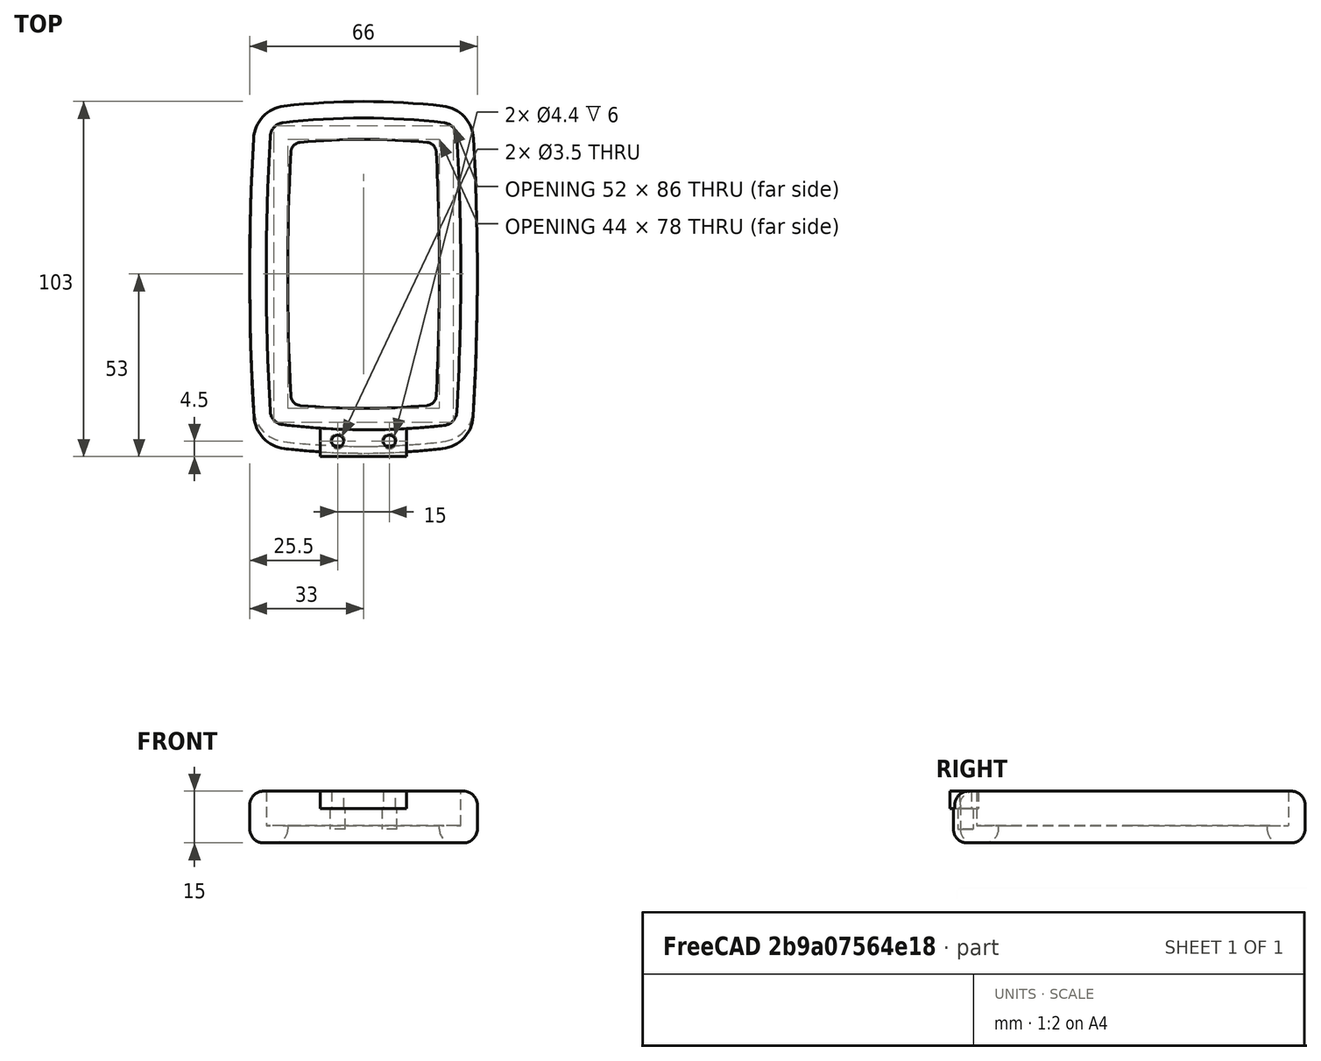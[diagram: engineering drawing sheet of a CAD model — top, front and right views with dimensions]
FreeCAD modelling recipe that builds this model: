
FCSTD DOCUMENT  (FreeCAD 0.20R29603 (Git))
Label: pad
License: All rights reserved
LicenseURL: http://en.wikipedia.org/wiki/All_rights_reserved
objects: Part::Cylinder×37, Part::MultiCommon×33, Part::Box×9, Part::Cut×8, Part::Fillet×7, Part::MultiFuse×2, Spreadsheet::Sheet×1, Mesh::Feature×1
note: 96 computed .brp shape members not serialized (recipe doc carries the construction recipe); baked Part::Feature solids carry a one-line shape summary decoded from their .brp

FEATURE [Part::Box] Box  label="Cube"
  AttacherType = Attacher::AttachEngine3D
  Height = 29
  Length = 60
  Placement = pos=(-29.77,-50.31,14) rot=(0,0,1;0rad)
  Width = 99
FEATURE [Part::Cylinder] Cylinder  label="Long Side circle"
  Angle = 360
  AttacherType = Attacher::AttachEngine3D
  FirstAngle = 0
  Height = 36
  Placement = pos=(671.8,0,0) rot=(0,0,1;0rad)
  Radius = 700
  SecondAngle = 0
  expr: .Placement.Base.x = Spreadsheet.B1 - 54 / 2 - Spreadsheet.B9
  expr: Radius = Spreadsheet.B1
FEATURE [Part::Cylinder] Cylinder001  label="Short side circle"
  Angle = 360
  AttacherType = Attacher::AttachEngine3D
  FirstAngle = 0
  Height = 53
  Placement = pos=(1,154.8,0) rot=(0,0,1;0rad)
  Radius = 200
  SecondAngle = 0
  expr: .Placement.Base.y = Spreadsheet.B2 - 88 / 2 - Spreadsheet.B9
  expr: Radius = Spreadsheet.B2
FEATURE [Part::MultiCommon] Common
  Shapes = -> [Box,Cylinder001]
FEATURE [Part::Cylinder] Cylinder002  label="Short side circle001"
  Angle = 360
  AttacherType = Attacher::AttachEngine3D
  FirstAngle = 0
  Height = 77
  Placement = pos=(-32,1,-262.75) rot=(0,1,0;1.5708rad)
  Radius = 310
  SecondAngle = 0
  expr: .Placement.Base.z = -(Spreadsheet.B3 - 31.25) + 16
  expr: Radius = Spreadsheet.B3
FEATURE [Part::MultiCommon] Common001
  Shapes = -> [Cylinder002,Common]
FEATURE [Part::MultiCommon] Common002
  Shapes = -> [Cylinder,Common001]
FEATURE [Part::Cylinder] Cylinder003  label="Short side circle002"
  Angle = 360
  AttacherType = Attacher::AttachEngine3D
  FirstAngle = 0
  Height = 36
  Placement = pos=(0,-154.8,0) rot=(0,0,1;0rad)
  Radius = 200
  SecondAngle = 0
  expr: .Placement.Base.y = -(Spreadsheet.B2 - 88 / 2) + Spreadsheet.B9
  expr: Radius = Spreadsheet.B2
FEATURE [Part::Cylinder] Cylinder004  label="Long Side circle001"
  Angle = 360
  AttacherType = Attacher::AttachEngine3D
  FirstAngle = 0
  Height = 36
  Placement = pos=(-671.8,0,0) rot=(0,0,1;0rad)
  Radius = 700
  SecondAngle = 0
  expr: .Placement.Base.x = -(Spreadsheet.B1 - 54 / 2) + Spreadsheet.B9
  expr: Radius = Spreadsheet.B1
FEATURE [Part::MultiCommon] Common003
  Shapes = -> [Cylinder004,Common002]
FEATURE [Part::MultiCommon] Common004
  Shapes = -> [Common003,Cylinder003]
FEATURE [Spreadsheet::Sheet] Spreadsheet
  cells = A1=long side; B1=700; F1=pad long side; G1=750; A2=short side; B2=200; F2=pad short side; G2=250; A3=top; B3=310; A4=center hole; B4=66; C4=27; D4=5; A5=Screw; B5=6.5; C5=3.5; A6=Screw head height; B6=3; A7=THreaded insert; B7=4.4; A9=earmuff margin; B9=1.2; A10=screwhole dist; B10=15
FEATURE [Part::Box] Box001  label="Cube001"
  AttacherType = Attacher::AttachEngine3D
  Height = 36
  Length = 60
  Placement = pos=(-29.77,-50.31,14) rot=(0,0,1;0rad)
  Width = 99
FEATURE [Part::Cylinder] Cylinder005  label="Long Side circle002"
  Angle = 360
  AttacherType = Attacher::AttachEngine3D
  FirstAngle = 0
  Height = 36
  Placement = pos=(678,0,0) rot=(0,0,1;0rad)
  Radius = 700
  SecondAngle = 0
  expr: .Placement.Base.x = Spreadsheet.B1 - 54 / 2 + 5
  expr: Radius = Spreadsheet.B1
FEATURE [Part::Cylinder] Cylinder006  label="Short side circle003"
  Angle = 360
  AttacherType = Attacher::AttachEngine3D
  FirstAngle = 0
  Height = 53
  Placement = pos=(0,161,0) rot=(0,0,1;0rad)
  Radius = 200
  SecondAngle = 0
  expr: .Placement.Base.y = Spreadsheet.B2 - 88 / 2 + 5
  expr: Radius = Spreadsheet.B2
FEATURE [Part::MultiCommon] Common005
  Shapes = -> [Box001,Cylinder006]
FEATURE [Part::Cylinder] Cylinder007  label="Short side circle004"
  Angle = 360
  AttacherType = Attacher::AttachEngine3D
  FirstAngle = 0
  Height = 77
  Placement = pos=(-32,0,0) rot=(0,1,0;1.5708rad)
  Radius = 310
  SecondAngle = 0
  expr: Radius = Spreadsheet.B3
FEATURE [Part::MultiCommon] Common006
  Shapes = -> [Cylinder007,Common005]
FEATURE [Part::MultiCommon] Common007
  Shapes = -> [Cylinder005,Common006]
FEATURE [Part::Cylinder] Cylinder008  label="Short side circle005"
  Angle = 360
  AttacherType = Attacher::AttachEngine3D
  FirstAngle = 0
  Height = 36
  Placement = pos=(0,-161,0) rot=(0,0,1;0rad)
  Radius = 200
  SecondAngle = 0
  expr: .Placement.Base.y = -(Spreadsheet.B2 - 88 / 2) - 5
  expr: Radius = Spreadsheet.B2
FEATURE [Part::Cylinder] Cylinder009  label="Long Side circle003"
  Angle = 360
  AttacherType = Attacher::AttachEngine3D
  FirstAngle = 0
  Height = 36
  Placement = pos=(-678,0,0) rot=(0,0,1;0rad)
  Radius = 700
  SecondAngle = 0
  expr: .Placement.Base.x = -(Spreadsheet.B1 - 54 / 2) - 5
  expr: Radius = Spreadsheet.B1
FEATURE [Part::MultiCommon] Common008
  Shapes = -> [Cylinder009,Common007]
FEATURE [Part::MultiCommon] Common009
  Shapes = -> [Common008,Cylinder008]
FEATURE [Mesh::Feature] Sccouter_Pad
  Placement = pos=(-33,50,-6) rot=(-1,0,0;4.71239rad)
FEATURE [Part::Fillet] Fillet  label="Center hole"
  Base = -> Common009
  Edges = 4 edges r=3: [Edge3,Edge5,Edge11,Edge15]
FEATURE [Part::Fillet] Fillet001  label="Pad cut"
  Base = -> Common004
  Edges = 4 edges r=4.2: [Edge3,Edge5,Edge11,Edge15]
  Placement = pos=(0,0,-15) rot=(0,0,1;0rad)
FEATURE [Part::Cylinder] Cylinder010  label="Short side circle006"
  Angle = 360
  AttacherType = Attacher::AttachEngine3D
  FirstAngle = 0
  Height = 36
  Placement = pos=(0,-150,0) rot=(0,0,1;0rad)
  Radius = 200
  SecondAngle = 0
  expr: .Placement.Base.y = -(Spreadsheet.G2 - 200 / 2)
  expr: Radius = Spreadsheet.B2
FEATURE [Part::Cylinder] Cylinder011  label="Long Side circle004"
  Angle = 360
  AttacherType = Attacher::AttachEngine3D
  FirstAngle = 0
  Height = 36
  Placement = pos=(-667,0,0) rot=(0,0,1;0rad)
  Radius = 700
  SecondAngle = 0
  expr: .Placement.Base.x = -(Spreadsheet.G1 - 166 / 2)
  expr: Radius = Spreadsheet.B1
FEATURE [Part::Cylinder] Cylinder012  label="Long Side circle005"
  Angle = 360
  AttacherType = Attacher::AttachEngine3D
  FirstAngle = 0
  Height = 36
  Placement = pos=(667,0,0) rot=(0,0,1;0rad)
  Radius = 700
  SecondAngle = 0
  expr: .Placement.Base.x = Spreadsheet.G1 - 166 / 2
  expr: Radius = Spreadsheet.B1
FEATURE [Part::Cylinder] Cylinder013  label="Short side circle007"
  Angle = 360
  AttacherType = Attacher::AttachEngine3D
  FirstAngle = 0
  Height = 53
  Placement = pos=(0,148,0) rot=(0,0,1;0rad)
  Radius = 200
  SecondAngle = 0
  expr: .Placement.Base.y = Spreadsheet.G2 - 200 / 2 - 2
  expr: Radius = Spreadsheet.B2
FEATURE [Part::Box] Box002  label="Cube002"
  AttacherType = Attacher::AttachEngine3D
  Height = 15
  Length = 110
  Placement = pos=(-48,-60,11) rot=(0,0,1;0rad)
  Width = 300
FEATURE [Part::MultiCommon] Common010
  Shapes = -> [Box002,Cylinder013]
FEATURE [Part::MultiCommon] Common011
  Shapes = -> [Cylinder012,Common010]
FEATURE [Part::MultiCommon] Common012
  Shapes = -> [Cylinder011,Common011]
FEATURE [Part::MultiCommon] Common013
  Placement = pos=(0,0,6) rot=(0,0,1;0rad)
  Shapes = -> [Common012,Cylinder010]
FEATURE [Part::Cut] Cut
  Base = -> Common013
  Placement = pos=(0,0,-23) rot=(0,0,1;0rad)
  Tool = -> Fillet
FEATURE [Part::Fillet] Fillet002
  Base = -> Cut
  Edges = 23 edges: [Edge2 r=4,Edge3 r=10,Edge4 r=4,Edge5 r=10,Edge6 r=4,Edge7 r=4,Edge8 r=4,Edge9 r=4,Edge10 r=4,Edge20 r=10,Edge21 r=4,Edge22 r=4,Edge23 r=4,Edge24 r=4,Edge25 r=4,Edge26 r=4,Edge27 r=4,Edge28 r=4,Edge29 r=4,Edge30 r=4,Edge31 r=4,Edge32 r=4,Edge33 r=10]
FEATURE [Part::Cut] Cut001  label="Pad pre cuts"
  Base = -> Fillet002
  Tool = -> Fillet001
FEATURE [Part::Cylinder] Cylinder014  label="Cylinder"
  Angle = 360
  AttacherType = Attacher::AttachEngine3D
  FirstAngle = 0
  Height = 10
  Placement = pos=(7.5,-47.5,0) rot=(0,0,1;0rad)
  Radius = 2.2
  SecondAngle = 0
  expr: .Placement.Base.x = Spreadsheet.B10 / 2
  expr: Radius = Spreadsheet.B7 / 2
FEATURE [Part::Cylinder] Cylinder015
  Angle = 360
  AttacherType = Attacher::AttachEngine3D
  FirstAngle = 0
  Height = 10
  Placement = pos=(-7.5,-47.5,0) rot=(0,0,1;0rad)
  Radius = 2.2
  SecondAngle = 0
  expr: .Placement.Base.x = -Spreadsheet.B10 / 2
  expr: Radius = Spreadsheet.B7 / 2
FEATURE [Part::MultiFuse] Fusion  label="Screw holes"
  Placement = pos=(0,-1,-2) rot=(0,0,1;0rad)
  Shapes = -> [Cylinder015,Cylinder014]
FEATURE [Part::Box] Box003  label="Cube003"
  AttacherType = Attacher::AttachEngine3D
  Height = 10
  Length = 25
  Placement = pos=(-12.5,-53,4) rot=(0,0,1;0rad)
  Width = 10
  expr: .Placement.Base.x = -(Spreadsheet.B10 + 10) / 2
  expr: Length = Spreadsheet.B10 + 10
FEATURE [Part::Box] Box004  label="Cube004"
  AttacherType = Attacher::AttachEngine3D
  Height = 5
  Length = 25
  Placement = pos=(-12.5,-53,4) rot=(0,0,1;0rad)
  Width = 10
  expr: .Placement.Base.x = -(Spreadsheet.B10 + 10) / 2
  expr: Length = Spreadsheet.B10 + 10
FEATURE [Part::Cut] Cut002
  Base = -> Cut001
  Tool = -> Box003
FEATURE [Part::Box] Box005  label="Cube005"
  AttacherType = Attacher::AttachEngine3D
  Height = 29
  Length = 60
  Placement = pos=(-29.77,-50.31,14) rot=(0,0,1;0rad)
  Width = 99
FEATURE [Part::Box] Box006  label="Cube006"
  AttacherType = Attacher::AttachEngine3D
  Height = 36
  Length = 60
  Placement = pos=(-29.77,-50.31,14) rot=(0,0,1;0rad)
  Width = 99
FEATURE [Part::Box] Box007  label="Cube007"
  AttacherType = Attacher::AttachEngine3D
  Height = 15
  Length = 110
  Placement = pos=(-48,-51,11) rot=(0,0,1;0rad)
  Width = 122
FEATURE [Part::Cylinder] Cylinder016  label="Long Side circle006"
  Angle = 360
  AttacherType = Attacher::AttachEngine3D
  FirstAngle = 0
  Height = 36
  Placement = pos=(671.8,0,0) rot=(0,0,1;0rad)
  Radius = 700
  SecondAngle = 0
  expr: .Placement.Base.x = Spreadsheet.B1 - 54 / 2 - Spreadsheet.B9
  expr: Radius = Spreadsheet.B1
FEATURE [Part::Cylinder] Cylinder017  label="Short side circle008"
  Angle = 360
  AttacherType = Attacher::AttachEngine3D
  FirstAngle = 0
  Height = 53
  Placement = pos=(1,154.8,0) rot=(0,0,1;0rad)
  Radius = 200
  SecondAngle = 0
  expr: .Placement.Base.y = Spreadsheet.B2 - 88 / 2 - Spreadsheet.B9
  expr: Radius = Spreadsheet.B2
FEATURE [Part::MultiCommon] Common014
  Shapes = -> [Box005,Cylinder017]
FEATURE [Part::Cylinder] Cylinder018  label="Short side circle009"
  Angle = 360
  AttacherType = Attacher::AttachEngine3D
  FirstAngle = 0
  Height = 77
  Placement = pos=(-32,1,-262.75) rot=(0,1,0;1.5708rad)
  Radius = 310
  SecondAngle = 0
  expr: .Placement.Base.z = -(Spreadsheet.B3 - 31.25) + 16
  expr: Radius = Spreadsheet.B3
FEATURE [Part::MultiCommon] Common015
  Shapes = -> [Cylinder018,Common014]
FEATURE [Part::MultiCommon] Common016
  Shapes = -> [Cylinder016,Common015]
FEATURE [Part::Cylinder] Cylinder019  label="Short side circle010"
  Angle = 360
  AttacherType = Attacher::AttachEngine3D
  FirstAngle = 0
  Height = 36
  Placement = pos=(0,-154.8,0) rot=(0,0,1;0rad)
  Radius = 200
  SecondAngle = 0
  expr: .Placement.Base.y = -(Spreadsheet.B2 - 88 / 2) + Spreadsheet.B9
  expr: Radius = Spreadsheet.B2
FEATURE [Part::Cylinder] Cylinder020  label="Long Side circle007"
  Angle = 360
  AttacherType = Attacher::AttachEngine3D
  FirstAngle = 0
  Height = 36
  Placement = pos=(-671.8,0,0) rot=(0,0,1;0rad)
  Radius = 700
  SecondAngle = 0
  expr: .Placement.Base.x = -(Spreadsheet.B1 - 54 / 2) + Spreadsheet.B9
  expr: Radius = Spreadsheet.B1
FEATURE [Part::MultiCommon] Common017
  Shapes = -> [Cylinder020,Common016]
FEATURE [Part::MultiCommon] Common018
  Shapes = -> [Common017,Cylinder019]
FEATURE [Part::Cylinder] Cylinder021  label="Long Side circle008"
  Angle = 360
  AttacherType = Attacher::AttachEngine3D
  FirstAngle = 0
  Height = 36
  Placement = pos=(678,0,0) rot=(0,0,1;0rad)
  Radius = 700
  SecondAngle = 0
  expr: .Placement.Base.x = Spreadsheet.B1 - 54 / 2 + 5
  expr: Radius = Spreadsheet.B1
FEATURE [Part::Cylinder] Cylinder022  label="Short side circle011"
  Angle = 360
  AttacherType = Attacher::AttachEngine3D
  FirstAngle = 0
  Height = 53
  Placement = pos=(0,161,0) rot=(0,0,1;0rad)
  Radius = 200
  SecondAngle = 0
  expr: .Placement.Base.y = Spreadsheet.B2 - 88 / 2 + 5
  expr: Radius = Spreadsheet.B2
FEATURE [Part::MultiCommon] Common019
  Shapes = -> [Box006,Cylinder022]
FEATURE [Part::Cylinder] Cylinder023  label="Short side circle012"
  Angle = 360
  AttacherType = Attacher::AttachEngine3D
  FirstAngle = 0
  Height = 77
  Placement = pos=(-32,0,0) rot=(0,1,0;1.5708rad)
  Radius = 310
  SecondAngle = 0
  expr: Radius = Spreadsheet.B3
FEATURE [Part::MultiCommon] Common020
  Shapes = -> [Cylinder023,Common019]
FEATURE [Part::MultiCommon] Common021
  Shapes = -> [Cylinder021,Common020]
FEATURE [Part::Cylinder] Cylinder024  label="Short side circle013"
  Angle = 360
  AttacherType = Attacher::AttachEngine3D
  FirstAngle = 0
  Height = 36
  Placement = pos=(0,-161,0) rot=(0,0,1;0rad)
  Radius = 200
  SecondAngle = 0
  expr: .Placement.Base.y = -(Spreadsheet.B2 - 88 / 2) - 5
  expr: Radius = Spreadsheet.B2
FEATURE [Part::Cylinder] Cylinder025  label="Long Side circle009"
  Angle = 360
  AttacherType = Attacher::AttachEngine3D
  FirstAngle = 0
  Height = 36
  Placement = pos=(-678,0,0) rot=(0,0,1;0rad)
  Radius = 700
  SecondAngle = 0
  expr: .Placement.Base.x = -(Spreadsheet.B1 - 54 / 2) - 5
  expr: Radius = Spreadsheet.B1
FEATURE [Part::MultiCommon] Common022
  Shapes = -> [Cylinder025,Common021]
FEATURE [Part::MultiCommon] Common023
  Shapes = -> [Common022,Cylinder024]
FEATURE [Part::Cylinder] Cylinder026  label="Short side circle014"
  Angle = 360
  AttacherType = Attacher::AttachEngine3D
  FirstAngle = 0
  Height = 36
  Placement = pos=(0,-150,0) rot=(0,0,1;0rad)
  Radius = 200
  SecondAngle = 0
  expr: .Placement.Base.y = -(Spreadsheet.G2 - 200 / 2)
  expr: Radius = Spreadsheet.B2
FEATURE [Part::Cylinder] Cylinder027  label="Long Side circle010"
  Angle = 360
  AttacherType = Attacher::AttachEngine3D
  FirstAngle = 0
  Height = 36
  Placement = pos=(-667,0,0) rot=(0,0,1;0rad)
  Radius = 700
  SecondAngle = 0
  expr: .Placement.Base.x = -(Spreadsheet.G1 - 166 / 2)
  expr: Radius = Spreadsheet.B1
FEATURE [Part::Cylinder] Cylinder028  label="Long Side circle011"
  Angle = 360
  AttacherType = Attacher::AttachEngine3D
  FirstAngle = 0
  Height = 36
  Placement = pos=(667,0,0) rot=(0,0,1;0rad)
  Radius = 700
  SecondAngle = 0
  expr: .Placement.Base.x = Spreadsheet.G1 - 166 / 2
  expr: Radius = Spreadsheet.B1
FEATURE [Part::Cylinder] Cylinder029  label="Short side circle015"
  Angle = 360
  AttacherType = Attacher::AttachEngine3D
  FirstAngle = 0
  Height = 53
  Placement = pos=(0,150,0) rot=(0,0,1;0rad)
  Radius = 200
  SecondAngle = 0
  expr: .Placement.Base.y = Spreadsheet.G2 - 200 / 2
  expr: Radius = Spreadsheet.B2
FEATURE [Part::MultiCommon] Common024
  Shapes = -> [Box007,Cylinder029]
FEATURE [Part::MultiCommon] Common025
  Shapes = -> [Cylinder028,Common024]
FEATURE [Part::MultiCommon] Common026
  Shapes = -> [Cylinder027,Common025]
FEATURE [Part::MultiCommon] Common027
  Placement = pos=(0,0,6) rot=(0,0,1;0rad)
  Shapes = -> [Common026,Cylinder026]
FEATURE [Part::Fillet] Fillet003  label="Center hole001"
  Base = -> Common023
  Edges = 4 edges r=3: [Edge3,Edge5,Edge11,Edge15]
FEATURE [Part::Cut] Cut003
  Base = -> Common027
  Placement = pos=(0,0,-23) rot=(0,0,1;0rad)
  Tool = -> Fillet003
FEATURE [Part::Fillet] Fillet004  label="Pad cut001"
  Base = -> Common018
  Edges = 4 edges r=4.2: [Edge3,Edge5,Edge11,Edge15]
  Placement = pos=(0,0,-15) rot=(0,0,1;0rad)
FEATURE [Part::Fillet] Fillet005
  Base = -> Cut003
  Edges = 23 edges: [Edge2 r=4,Edge3 r=10,Edge4 r=4,Edge5 r=10,Edge6 r=4,Edge7 r=4,Edge8 r=4,Edge9 r=4,Edge10 r=4,Edge20 r=10,Edge21 r=4,Edge22 r=4,Edge23 r=4,Edge24 r=4,Edge25 r=4,Edge26 r=4,Edge27 r=4,Edge28 r=4,Edge29 r=4,Edge30 r=4,Edge31 r=4,Edge32 r=4,Edge33 r=10]
FEATURE [Part::Cut] Cut004  label="Pad pre cuts001"
  Base = -> Fillet005
  Tool = -> Fillet004
FEATURE [Part::Cut] Cut005  label="pad with holes"
  Base = -> Cut002
  Tool = -> Fusion
FEATURE [Part::Box] Box008  label="Cube008"
  AttacherType = Attacher::AttachEngine3D
  Height = 29
  Length = 60
  Placement = pos=(-29.77,-50.31,14) rot=(0,0,1;0rad)
  Width = 99
FEATURE [Part::Cylinder] Cylinder030  label="Long Side circle012"
  Angle = 360
  AttacherType = Attacher::AttachEngine3D
  FirstAngle = 0
  Height = 36
  Placement = pos=(671.8,0,0) rot=(0,0,1;0rad)
  Radius = 700
  SecondAngle = 0
  expr: .Placement.Base.x = Spreadsheet.B1 - 54 / 2 - Spreadsheet.B9
  expr: Radius = Spreadsheet.B1
FEATURE [Part::Cylinder] Cylinder031  label="Short side circle016"
  Angle = 360
  AttacherType = Attacher::AttachEngine3D
  FirstAngle = 0
  Height = 53
  Placement = pos=(1,154.8,0) rot=(0,0,1;0rad)
  Radius = 200
  SecondAngle = 0
  expr: .Placement.Base.y = Spreadsheet.B2 - 88 / 2 - Spreadsheet.B9
  expr: Radius = Spreadsheet.B2
FEATURE [Part::MultiCommon] Common028
  Shapes = -> [Box008,Cylinder031]
FEATURE [Part::Cylinder] Cylinder032  label="Short side circle017"
  Angle = 360
  AttacherType = Attacher::AttachEngine3D
  FirstAngle = 0
  Height = 77
  Placement = pos=(-32,1,-262.75) rot=(0,1,0;1.5708rad)
  Radius = 310
  SecondAngle = 0
  expr: .Placement.Base.z = -(Spreadsheet.B3 - 31.25) + 16
  expr: Radius = Spreadsheet.B3
FEATURE [Part::MultiCommon] Common029
  Shapes = -> [Cylinder032,Common028]
FEATURE [Part::MultiCommon] Common030
  Shapes = -> [Cylinder030,Common029]
FEATURE [Part::Cylinder] Cylinder033  label="Short side circle018"
  Angle = 360
  AttacherType = Attacher::AttachEngine3D
  FirstAngle = 0
  Height = 36
  Placement = pos=(0,-154.8,0) rot=(0,0,1;0rad)
  Radius = 200
  SecondAngle = 0
  expr: .Placement.Base.y = -(Spreadsheet.B2 - 88 / 2) + Spreadsheet.B9
  expr: Radius = Spreadsheet.B2
FEATURE [Part::Cylinder] Cylinder034  label="Long Side circle013"
  Angle = 360
  AttacherType = Attacher::AttachEngine3D
  FirstAngle = 0
  Height = 36
  Placement = pos=(-671.8,0,0) rot=(0,0,1;0rad)
  Radius = 700
  SecondAngle = 0
  expr: .Placement.Base.x = -(Spreadsheet.B1 - 54 / 2) + Spreadsheet.B9
  expr: Radius = Spreadsheet.B1
FEATURE [Part::MultiCommon] Common031
  Shapes = -> [Cylinder034,Common030]
FEATURE [Part::MultiCommon] Common032
  Shapes = -> [Common031,Cylinder033]
FEATURE [Part::Fillet] Fillet006  label="Pad cut002"
  Base = -> Common032
  Edges = 4 edges r=4.2: [Edge3,Edge5,Edge11,Edge15]
  Placement = pos=(0,0,-15) rot=(0,0,1;0rad)
FEATURE [Part::Cut] Cut006
  Base = -> Box004
  Tool = -> Fillet006
FEATURE [Part::Cylinder] Cylinder035
  Angle = 360
  AttacherType = Attacher::AttachEngine3D
  FirstAngle = 0
  Height = 10
  Placement = pos=(7.5,-47.5,0) rot=(0,0,1;0rad)
  Radius = 1.75
  SecondAngle = 0
  expr: .Placement.Base.x = Spreadsheet.B10 / 2
  expr: Radius = Spreadsheet.C5 / 2
FEATURE [Part::Cylinder] Cylinder036
  Angle = 360
  AttacherType = Attacher::AttachEngine3D
  FirstAngle = 0
  Height = 10
  Placement = pos=(-7.5,-47.5,0) rot=(0,0,1;0rad)
  Radius = 1.75
  SecondAngle = 0
  expr: .Placement.Base.x = -Spreadsheet.B10 / 2
  expr: Radius = Spreadsheet.C5 / 2
FEATURE [Part::MultiFuse] Fusion001  label="Screw holes001"
  Placement = pos=(0,-1,1) rot=(0,0,1;0rad)
  Shapes = -> [Cylinder036,Cylinder035]
FEATURE [Part::Cut] Cut007  label="band attachement"
  Base = -> Cut006
  Tool = -> Fusion001
